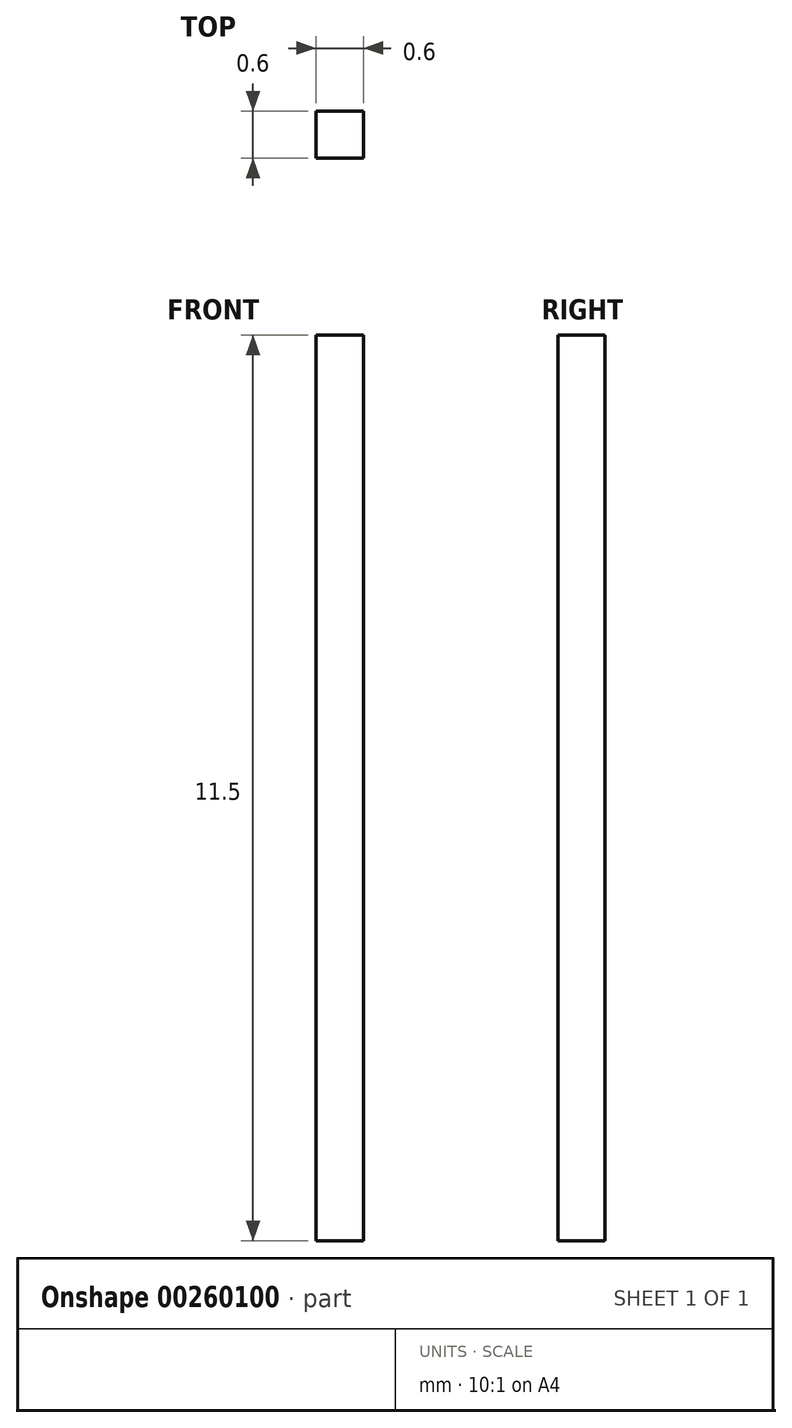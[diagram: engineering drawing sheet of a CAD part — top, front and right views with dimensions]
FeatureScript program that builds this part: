
annotation { "Feature Type Name" : "Feature", "Feature Type Description" : "" }
export const myFeature = defineFeature(function(context is Context, id is Id, definition is map)
    precondition{}
    {
        {
            var Q0;
            Q0=qCreatedBy(makeId("Top.planeOp"),FACE);
            var sketch = newSketch(context, id + "F0", { "sketchPlane" : qUnion([Q0])});
            skLineSegment(sketch, "E0.bottom", {"start": v(0, 0) * mm, "end": v(0.6, 0) * mm});
            skLineSegment(sketch, "E0.top", {"start": v(0, 0.6) * mm, "end": v(0.6, 0.6) * mm});
            skLineSegment(sketch, "E0.left", {"start": v(0, 0) * mm, "end": v(0, 0.6) * mm});
            skLineSegment(sketch, "E0.right", {"start": v(0.6, 0) * mm, "end": v(0.6, 0.6) * mm});
            skSolve(sketch);
        }
        {
            var Q0;
            Q0 = qSketchRegion(id + "F0", true);
            extrude(context, id + "F1", {"entities" : qUnion([Q0]), "depth" : 11.5 * mm});
        }
    });
